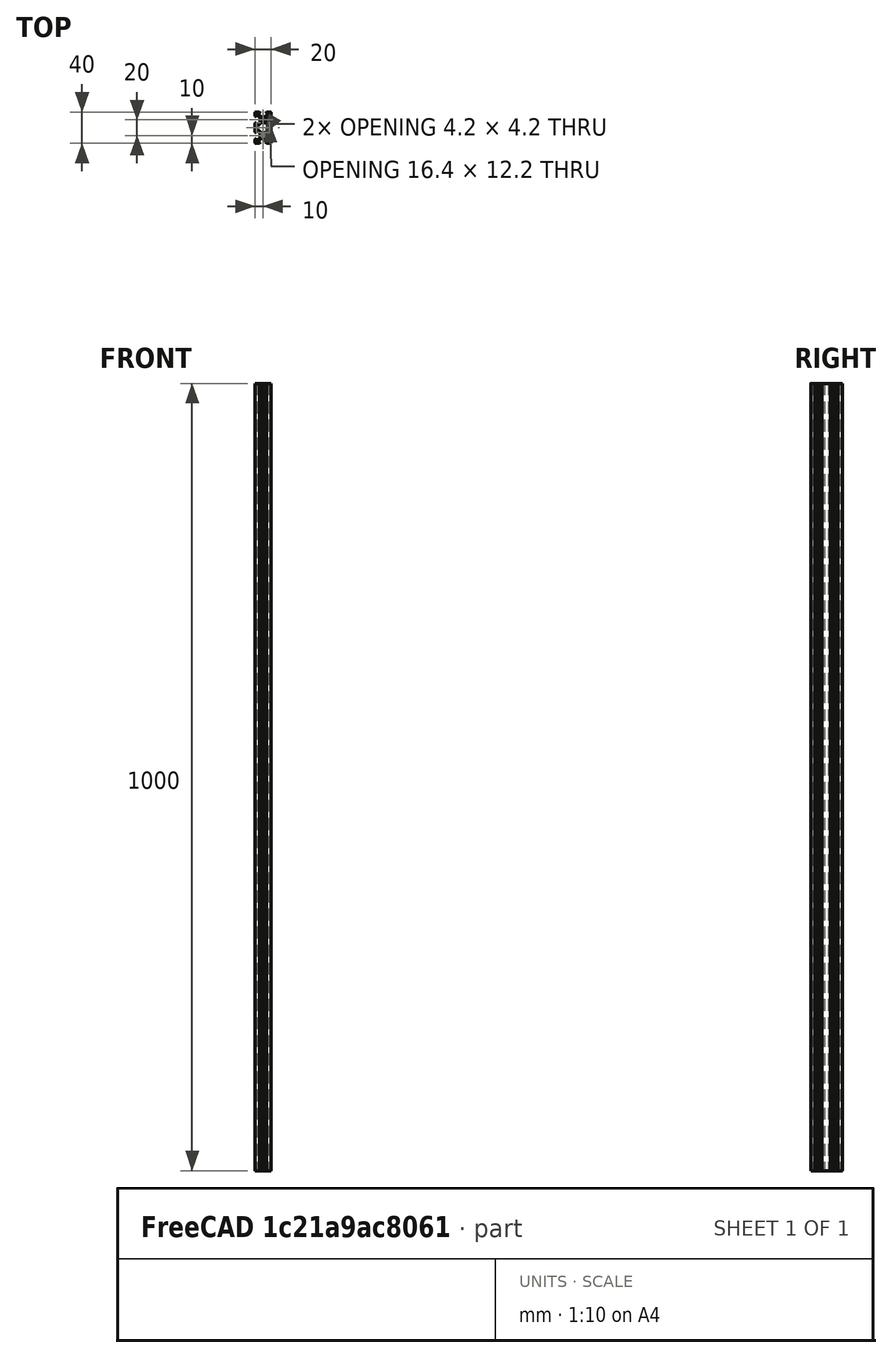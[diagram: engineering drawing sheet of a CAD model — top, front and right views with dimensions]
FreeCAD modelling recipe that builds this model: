
FCSTD DOCUMENT  (FreeCAD 2022.430R26244 +4758 (Git))
Label: as3V-Slot 20x40x1000 Linear Rail
License: All rights reserved
LicenseURL: http://en.wikipedia.org/wiki/All_rights_reserved
objects: Part::FeaturePython×5, App::FeaturePython×2, Part::Feature×1
note: 5 computed .brp shape members not serialized (recipe doc carries the construction recipe); baked Part::Feature solids carry a one-line shape summary decoded from their .brp

FEATURE [Part::Feature] Solid  label="V-Slot 20x40x1000 Linear Rail"
  TreeRank = 0
  shape: bbox 20 x 40 x 1000 mm, 116 faces (baked)
FEATURE [App::FeaturePython] Constraints  # WARN: FeaturePython — macro-defined, semantics opaque (R4)
  TreeRank = 0
  _LinkVersion = 1
  _Version = 1
FEATURE [Part::FeaturePython] Parts  # WARN: FeaturePython — macro-defined, semantics opaque (R4)
  Group = -> [Solid]
  GroupMode = 0
  TreeRank = 0
  _LinkVersion = 1
FEATURE [Part::FeaturePython] Assembly  label="As3V-Slot 20x40x1000 Linear Rail"  # WARN: FeaturePython — macro-defined, semantics opaque (R4)
  AutoRelax = true
  BuildShape = 0
  Freeze = false
  Group = -> [Constraints,Elements,Parts]
  TreeRank = 0
  Verbose = false
  _LinkVersion = 1
  _SolverType = 1
  _Version = 1
FEATURE [App::FeaturePython] Elements  # WARN: FeaturePython — macro-defined, semantics opaque (R4)
  Group = -> [Element,Element001,Element002]
  TreeRank = 0
  _LinkVersion = 1
FEATURE [Part::FeaturePython] Element  label="Etrem1"  # link proxy (typed FeaturePython)
  Detach = false
  LinkTransform = true
  LinkedObject = -> Solid [Face116]
  TreeRank = 0
  _LinkVersion = 1
  _Parent = -> Elements
FEATURE [Part::FeaturePython] Element001  label="Lat1"  # link proxy (typed FeaturePython)
  Detach = false
  LinkTransform = true
  LinkedObject = -> Solid [Face62]
  TreeRank = 0
  _LinkVersion = 1
  _Parent = -> Elements
FEATURE [Part::FeaturePython] Element002  label="FaceRef"  # link proxy (typed FeaturePython)
  Detach = false
  LinkTransform = true
  LinkedObject = -> Solid [Face45]
  TreeRank = 0
  _LinkVersion = 1
  _Parent = -> Elements
